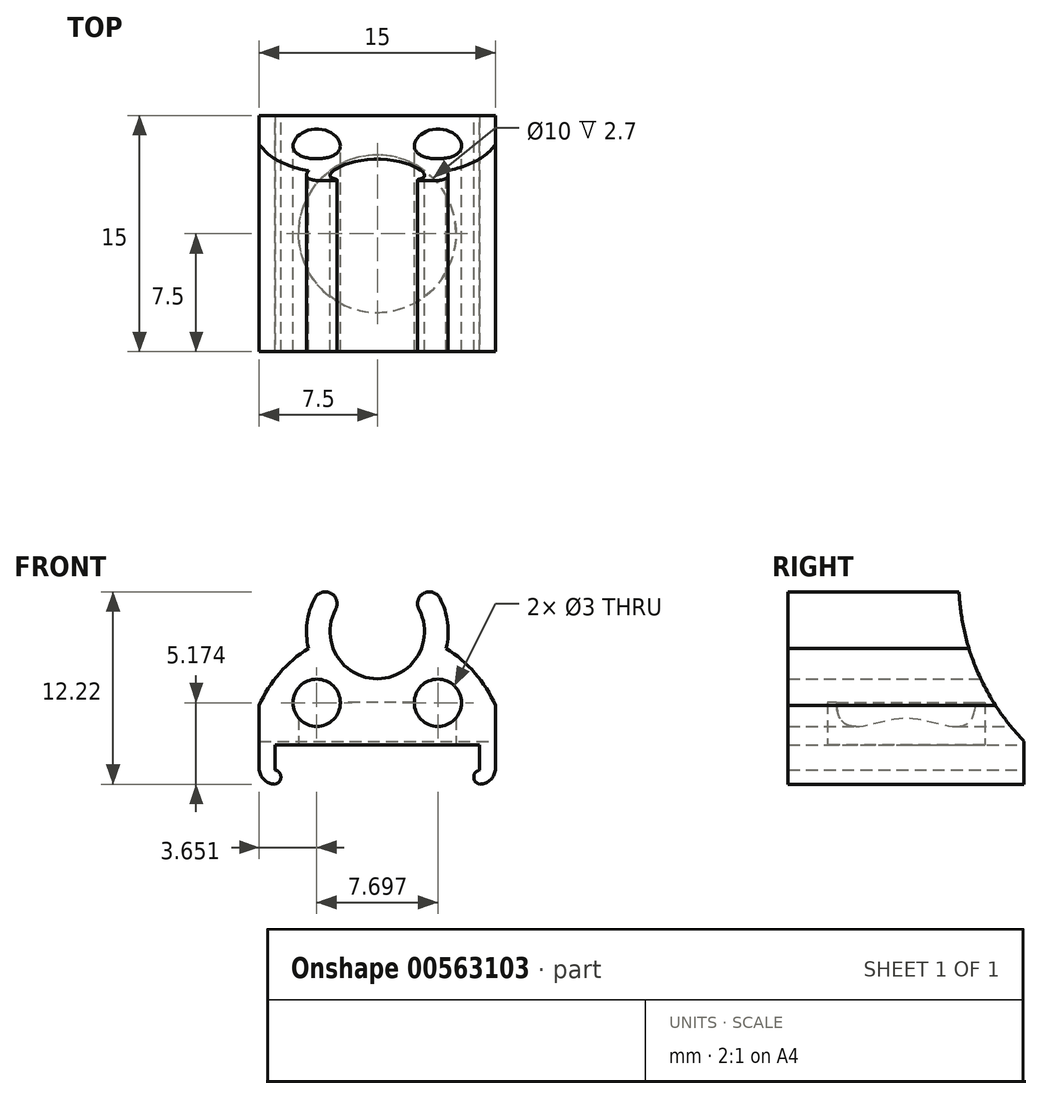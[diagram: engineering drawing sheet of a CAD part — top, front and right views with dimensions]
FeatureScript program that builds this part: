
annotation { "Feature Type Name" : "Feature", "Feature Type Description" : "" }
export const myFeature = defineFeature(function(context is Context, id is Id, definition is map)
    precondition{}
    {
        {
            var Q0;
            Q0=qCreatedBy(makeId("Front.planeOp"),FACE);
            var sketch = newSketch(context, id + "F0", { "sketchPlane" : qUnion([Q0])});
            skLineSegment(sketch, "E0.top", {"start": v(-6.5, 0.8) * mm, "end": v(6.5, 0.8) * mm});
            skLineSegment(sketch, "E0.left", {"start": v(-6.5, -0.8) * mm, "end": v(-6.5, 0.8) * mm});
            skPoint(sketch, "E0.middle", {"position": v(0, 0) * mm});
            skLineSegment(sketch, "E1.bottom", {"start": v(-6.5, -1.7) * mm, "end": v(-6.5, -1.7) * mm});
            skLineSegment(sketch, "E1.left", {"start": v(-7.5, -0.7) * mm, "end": v(-7.5, 3.3) * mm});
            skPoint(sketch, "E1.middle", {"position": v(-6.5, 0.8) * mm});
            skArc(sketch, "E2", {"start": v(-7.5, 3.3) * mm, "mid": v(-6.2, 5.35) * mm, "end": v(-4.37, 6.93) * mm});
            skPoint(sketch, "E3.endSnap0", {"position": v(-6.5, 0) * mm});
            skPoint(sketch, "E4.visualSharp", {"position": v(-7.5, -1.7) * mm});
            skArc(sketch, "E4.filletArc", {"start": v(-7.5, -0.7) * mm, "mid": v(-7.2, -1.4) * mm, "end": v(-6.5, -1.7) * mm});
            skArc(sketch, "E5", {"start": v(-6.67, -1.7) * mm, "mid": v(-6.13, -1.33) * mm, "end": v(-6.5, -0.8) * mm});
            skPoint(sketch, "E5.second.point", {"position": v(-6.5, -1.7) * mm});
            skPoint(sketch, "E6.MirrorCS.end.orphan", {"position": v(7.5, 3.3) * mm});
            skLineSegment(sketch, "E7.MirrorCS", {"start": v(6.5, -0.8) * mm, "end": v(6.5, 0.8) * mm});
            skArc(sketch, "E8.MirrorCS", {"start": v(6.67, -1.7) * mm, "mid": v(6.13, -1.33) * mm, "end": v(6.5, -0.8) * mm});
            skArc(sketch, "E9.MirrorCS", {"start": v(7.5, -0.7) * mm, "mid": v(7.2, -1.4) * mm, "end": v(6.5, -1.7) * mm});
            skLineSegment(sketch, "E10.MirrorCS", {"start": v(7.5, -0.7) * mm, "end": v(7.5, 3.3) * mm});
            skLineSegment(sketch, "E11", {"start": v(0, 0) * mm, "end": v(0, 8) * mm, "construction": true});
            skArc(sketch, "E12", {"start": v(-2.64, 9.42) * mm, "mid": v(0, 5) * mm, "end": v(2.64, 9.42) * mm});
            skArc(sketch, "E13", {"start": v(4.37, 6.93) * mm, "mid": v(4.46, 8.56) * mm, "end": v(3.97, 10.12) * mm});
            skArc(sketch, "E14.trimOffspring", {"start": v(4.37, 6.93) * mm, "mid": v(6.2, 5.35) * mm, "end": v(7.5, 3.3) * mm});
            skArc(sketch, "E15.trimOffspring", {"start": v(-3.97, 10.12) * mm, "mid": v(-4.46, 8.56) * mm, "end": v(-4.37, 6.93) * mm});
            skArc(sketch, "E16", {"start": v(-2.64, 9.42) * mm, "mid": v(-2.95, 10.43) * mm, "end": v(-3.97, 10.12) * mm});
            skArc(sketch, "E17.MirrorCS", {"start": v(2.64, 9.42) * mm, "mid": v(2.95, 10.43) * mm, "end": v(3.97, 10.12) * mm});
            skCircle(sketch, "E18", {"center": v(-3.85, 3.47) * mm, "radius": 1.5 * mm});
            skCircle(sketch, "E19.MirrorC", {"center": v(3.85, 3.47) * mm, "radius": 1.5 * mm});
            skSolve(sketch);
        }
        {
            var Q0;
            Q0=makeQuery(id+"F0.imprint","IMPRINT",FACE,{"disambiguationData":[TD([[makeQuery(id+"F0.imprint","IMPRINT",EDGE,{"derivedFrom":sQuery(id+"F0.wireOp",EDGE,"E0.top")}),1.0]])]});
            extrude(context, id + "F1", {"entities" : qUnion([Q0]), "depth" : 15 * mm, "offsetDistance" : 25 * mm});
        }
        {
            var Q0;
            Q0=qCreatedBy(makeId("Right.planeOp"),FACE);
            var sketch = newSketch(context, id + "F2", { "sketchPlane" : qUnion([Q0])});
            skCircle(sketch, "E20", {"center": v(10.4, 11.2) * mm, "radius": 14.55 * mm});
            skLineSegment(sketch, "E21", {"start": v(0, 0) * mm, "end": v(-7.5, 0) * mm, "construction": true});
            skLineSegment(sketch, "E22", {"start": v(-7.5, 0) * mm, "end": v(-7.5, 16.3) * mm, "construction": true});
            skCircle(sketch, "E23.MirrorC", {"center": v(-25.4, 11.2) * mm, "radius": 14.55 * mm});
            skSolve(sketch);
        }
        {
            var Q0;
            Q0=makeQuery(id+"F2.imprint","IMPRINT",FACE,{"disambiguationData":[TD([[makeQuery(id+"F2.imprint","IMPRINT",EDGE,{"derivedFrom":sQuery(id+"F2.wireOp",EDGE,"E23.MirrorC")}),-1.0]])]});
            var Q1;
            Q1=makeQuery(id+"F2.imprint","IMPRINT",FACE,{"disambiguationData":[TD([[makeQuery(id+"F2.imprint","IMPRINT",EDGE,{"derivedFrom":sQuery(id+"F2.wireOp",EDGE,"E20")}),1.0]])]});
            extrude(context, id + "F3", {"entities" : qUnion([Q0, Q1]), "operationType" : NewBodyOperationType.REMOVE, "oppositeDirection" : true, "depth" : 25 * mm, "offsetDistance" : 25 * mm, "hasSecondDirection" : true, "secondDirectionOppositeDirection" : false, "secondDirectionDepth" : 25 * mm});
        }
        {
            var Q0;
            Q0=qCreatedBy(makeId("Top.planeOp"),FACE);
            var sketch = newSketch(context, id + "F4", { "sketchPlane" : qUnion([Q0])});
            skLineSegment(sketch, "E24", {"start": v(0, 0) * mm, "end": v(0, -7.5) * mm, "construction": true});
            skCircle(sketch, "E25", {"center": v(0, -7.5) * mm, "radius": 5 * mm});
            skSolve(sketch);
        }
        {
            var Q0;
            Q0=makeQuery(id+"F4.imprint","IMPRINT",FACE,{"disambiguationData":[TD([[makeQuery(id+"F4.imprint","IMPRINT",EDGE,{"derivedFrom":sQuery(id+"F4.wireOp",EDGE,"E25")}),1.0]])]});
            extrude(context, id + "F5", {"entities" : qUnion([Q0]), "operationType" : NewBodyOperationType.REMOVE, "depth" : 3.5 * mm, "offsetDistance" : 25 * mm});
        }
    });
